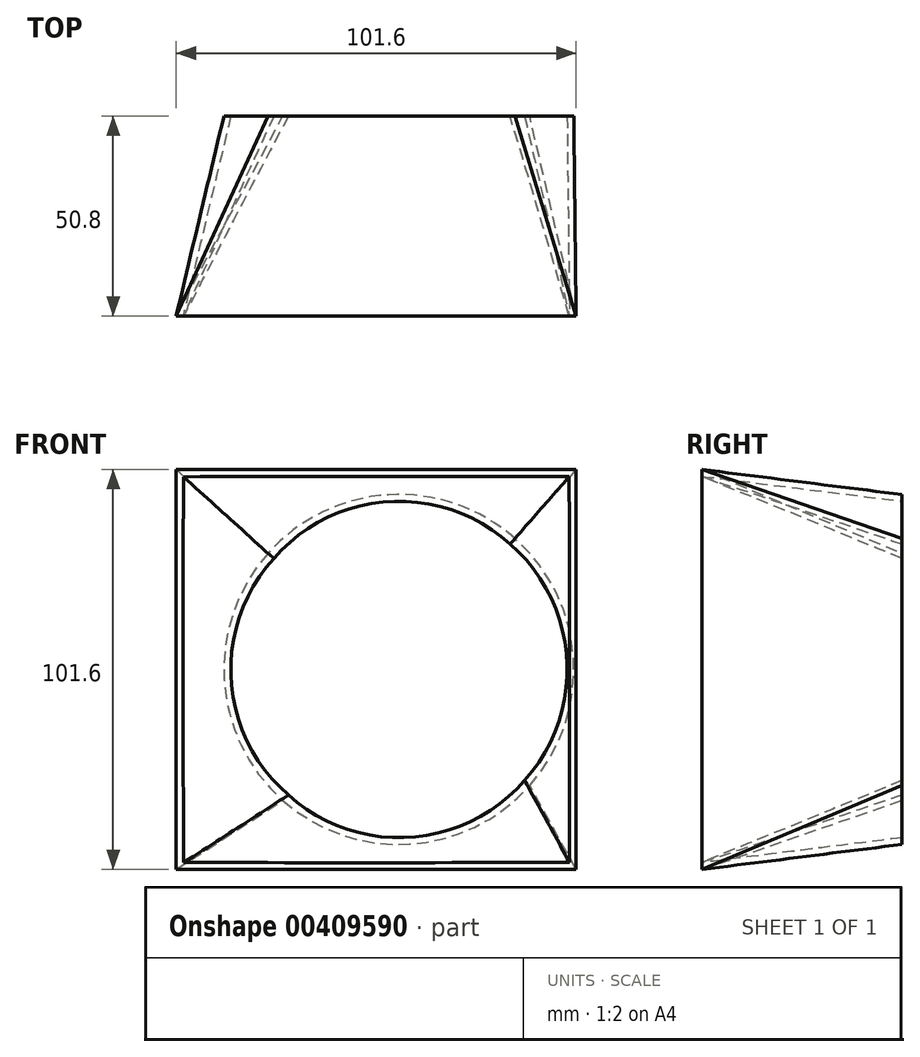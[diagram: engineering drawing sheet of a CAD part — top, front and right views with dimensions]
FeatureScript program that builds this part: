
annotation { "Feature Type Name" : "Feature", "Feature Type Description" : "" }
export const myFeature = defineFeature(function(context is Context, id is Id, definition is map)
    precondition{}
    {
        {
            var Q0;
            Q0=qCreatedBy(makeId("Front.planeOp"),FACE);
            var sketch = newSketch(context, id + "F0", { "sketchPlane" : qUnion([Q0])});
            skCircle(sketch, "E0", {"center": v(5.77, 0) * mm, "radius": 44.45 * mm});
            skSolve(sketch);
        }
        {
            var Q0;
            Q0=qCreatedBy(makeId("Front.planeOp"),FACE);
            cPlane(context, id + "F1", {"entities" : qUnion([Q0]), "cplaneType" : CPlaneType.OFFSET, "offset" : 50.8 * mm, "width" : 152.4 * mm, "height" : 152.4 * mm});
        }
        {
            var Q0;
            Q0=qCreatedBy(id+"F1.planeOp",FACE);
            var sketch = newSketch(context, id + "F2", { "sketchPlane" : qUnion([Q0])});
            skLineSegment(sketch, "E1.bottom", {"start": v(50.8, 50.8) * mm, "end": v(-50.8, 50.8) * mm});
            skLineSegment(sketch, "E1.top", {"start": v(50.8, -50.8) * mm, "end": v(-50.8, -50.8) * mm});
            skLineSegment(sketch, "E1.left", {"start": v(50.8, 50.8) * mm, "end": v(50.8, -50.8) * mm});
            skLineSegment(sketch, "E1.right", {"start": v(-50.8, 50.8) * mm, "end": v(-50.8, -50.8) * mm});
            skPoint(sketch, "E1.middle", {"position": v(0, 0) * mm});
            skSolve(sketch);
        }
        {
            var Q0;
            Q0=makeQuery(id+"F2.imprint","IMPRINT",FACE,{"disambiguationData":[TD([[makeQuery(id+"F2.imprint","IMPRINT",EDGE,{"derivedFrom":sQuery(id+"F2.wireOp",EDGE,"E1.bottom")}),1.0]])]});
            var Q1;
            Q1=makeQuery(id+"F0.imprint","IMPRINT",FACE,{"disambiguationData":[TD([[makeQuery(id+"F0.imprint","IMPRINT",EDGE,{"derivedFrom":sQuery(id+"F0.wireOp",EDGE,"E0")}),1.0]])]});
            loft(context, id + "F3", {"sheetProfilesArray" : [{ "sheetProfileEntities" : qUnion([Q0]) }, { "sheetProfileEntities" : qUnion([Q1]) }]});
        }
        {
            var Q0;
            Q0=makeQuery(id+"F3.opLoft","CAP_FACE",FACE,{"disambiguationData":[OSD([makeQuery(id+"F2.imprint","IMPRINT",FACE,{"disambiguationData":[TD([[makeQuery(id+"F2.imprint","IMPRINT",EDGE,{"derivedFrom":sQuery(id+"F2.wireOp",EDGE,"E1.bottom")}),1.0]])]})])],"isStart":true});
            var Q1;
            Q1=makeQuery(id+"F3.opLoft","CAP_FACE",FACE,{"disambiguationData":[OSD([makeQuery(id+"F0.imprint","IMPRINT",FACE,{"disambiguationData":[TD([[makeQuery(id+"F0.imprint","IMPRINT",EDGE,{"derivedFrom":sQuery(id+"F0.wireOp",EDGE,"E0")}),1.0]])]})])],"isStart":true});
            shell(context, id + "F4", {"entities" : qUnion([Q0, Q1]), "thickness" : 1.7 * mm});
        }
    });
